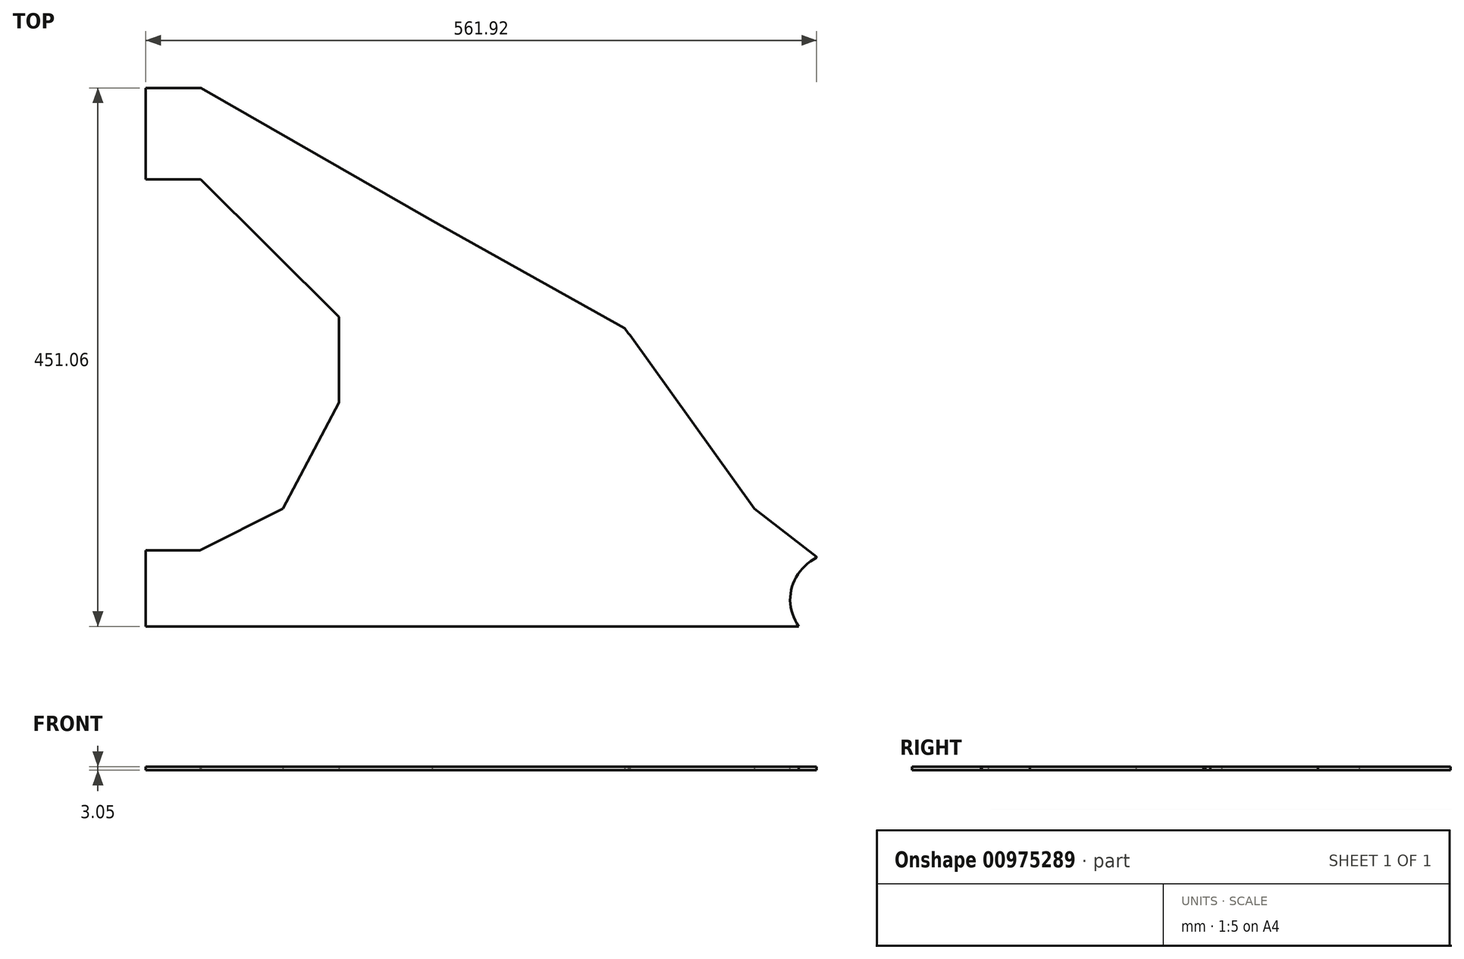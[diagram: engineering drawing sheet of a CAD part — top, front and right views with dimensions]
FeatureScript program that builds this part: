
annotation { "Feature Type Name" : "Feature", "Feature Type Description" : "" }
export const myFeature = defineFeature(function(context is Context, id is Id, definition is map)
    precondition{}
    {
        {
            var Q0;
            Q0=qCreatedBy(makeId("Top.planeOp"),FACE);
            var sketch = newSketch(context, id + "F0", { "sketchPlane" : qUnion([Q0])});
            skLineSegment(sketch, "E0", {"start": v(-280.96, 225.53) * mm, "end": v(-234.68, 225.53) * mm});
            skLineSegment(sketch, "E1", {"start": v(-280.96, 149.12) * mm, "end": v(-280.96, 225.53) * mm});
            skLineSegment(sketch, "E2", {"start": v(-280.96, 149.12) * mm, "end": v(-235.16, 149.12) * mm});
            skLineSegment(sketch, "E3", {"start": v(-235.16, 149.12) * mm, "end": v(-119.05, 33.92) * mm});
            skLineSegment(sketch, "E4", {"start": v(-119.05, 33.92) * mm, "end": v(-119.05, -37.97) * mm});
            skLineSegment(sketch, "E5", {"start": v(-166.04, -126.92) * mm, "end": v(-119.05, -37.97) * mm});
            skLineSegment(sketch, "E6", {"start": v(-235.7, -161.82) * mm, "end": v(-166.04, -126.92) * mm});
            skLineSegment(sketch, "E7", {"start": v(-280.96, -161.82) * mm, "end": v(-235.7, -161.82) * mm});
            skLineSegment(sketch, "E8", {"start": v(-280.96, -225.53) * mm, "end": v(-280.96, -161.82) * mm});
            skLineSegment(sketch, "E9", {"start": v(-280.96, -225.53) * mm, "end": v(123.1, -225.53) * mm});
            skLineSegment(sketch, "E10", {"start": v(120.42, 24.21) * mm, "end": v(123.1, 20.07) * mm});
            skLineSegment(sketch, "E11", {"start": v(-40.96, 114.46) * mm, "end": v(120.42, 24.21) * mm});
            skLineSegment(sketch, "E12", {"start": v(-234.68, 225.53) * mm, "end": v(-40.96, 114.46) * mm});
            skLineSegment(sketch, "E13", {"start": v(124.7, -225.53) * mm, "end": v(123.1, -225.53) * mm});
            skLineSegment(sketch, "E14", {"start": v(123.1, 20.07) * mm, "end": v(124, 19.2) * mm});
            skLineSegment(sketch, "E15", {"start": v(124, 19.2) * mm, "end": v(124.7, 18.6) * mm});
            skLineSegment(sketch, "E16", {"start": v(124.7, 18.6) * mm, "end": v(228.94, -126.8) * mm});
            skLineSegment(sketch, "E17", {"start": v(124.7, -225.53) * mm, "end": v(266.08, -225.53) * mm});
            skEllipticalArc(sketch, "E18", {});
            skLineSegment(sketch, "E19", {"start": v(280.96, -167.8) * mm, "end": v(280.96, -167.27) * mm});
            skLineSegment(sketch, "E20", {"start": v(228.94, -126.8) * mm, "end": v(280.96, -167.27) * mm});
            const initialGuessF0  = {"E18": [0.304381535, -0.2032, 1.792989, 0, 0.0455419206, 0.041275, 2.111008, 3.713127]};
            skSetInitialGuess(sketch, initialGuessF0);
            skSolve(sketch);
        }
        {
            var Q0;
            Q0 = qSketchRegion(id + "F0", true);
            extrude(context, id + "F1", {"entities" : qUnion([Q0]), "depth" : 3.05 * mm, "offsetDistance" : 25.4 * mm});
        }
    });
